# Revit family: NBS_Allermuir_DmstcChrs_Tarry_LoungeChair
name_source: partatom
category: Furniture
revit_build: Autodesk Revit 2017 (Build: 20171027_0315(x64)
units: mm (PartAtom-declared; Revit-internal decimal feet)

## family parameters
Always vertical = Yes
Cut with Voids When Loaded = No
Room Calculation Point = No
Shared = No
Work Plane-Based = No

## types (2) — shared parameters
AssetType = Movable
Category = Pr_40_50_12_22:Dining chairs
CodePerformance = ANSI/BIFMA X5.1: 2017
DurationUnit = year
EnvironmentalProductDeclaration = http://www.thesenatorgroup.com
ExpectedLife = 10
Features = Moulded foam construction with dual density back foam, height adjustable headrest, fully upholstered, solid ash legs with a clear finish, plastic glides,, optional feature: solid ash legs can be stained or colour washed , optional feature: plastic glides with felt, optional feature: two-tone upholstery
FrameColour = Black
FrameFinish = Powder coat
FramesFinish = Clear
FramesMaterial = Solid ash
IfcExportAs = IfcFurnitureType
IfcExportType = CHAIR
IntegralAccessories = Plastic glides
IsBuiltIn = No
ManufacturerName = Allermuir
ManufacturerURL = http://www.allermuir.co.uk
ModelReference = TarryLoungeChair
NBSCertification = www.nationalbimlibrary.com/cert/y25tegts
NBSDescription = Domestic chairs
NBSReference = 45-35-20/365
NominalDepth = 815 mm  [stored 2.67388 ft]
NominalLength = 740 mm  [stored 2.42782 ft]
NominalWidth = 740 mm  [stored 2.42782 ft]
ProductInformation = http://www.allermuir.co.uk
SeatBaseMaterial = NBS_Concept
SeatFrameMaterial = NBS_Concept
SeatingSeatMaterial = NBS_Concept
SeatsAndBacksFinish = Upholstered
SeatsAndBacksMaterial = Upholstered
Status = New
Style = Chair
Uniclass2015Code = Pr_40_50_12_22
Uniclass2015Title = Dining chairs
Uniclass2015Version = Products v1.12
Version = 2
WarrantyDescription = Allermuir warrant that its manufactured products are free from manufacturing defects - in materials or workmanship - for a period of five (5) years. , Allermuir will repair, or replace (at Allermuir's sole discretion) with comparable free of charge materials / components, any product / component which fails under normal use in a single shift environment, as a result of a defect in the materials and/ or workmanship
WarrantyDurationParts = 5
WarrantyDurationUnit = year
Weight = 33 kg
zero-valued in all types: HighestSeatingHeight, LowestSeatingHeight

## per-type parameters (varying)
| type | BIMObjectName | Description | Has4StarSwivelBase | HasWoodLegs | Name | NominalHeight | SeatingHeight | Size |
| TAR405 | NBS_Allermuir_DomesticChairs_TarryLoungeChair_TAR405 | Lounge chair 4-Star Swivel Base | Yes | No | DomesticChairs_TarryLoungeChair_TAR405_Allermuir | 1210 mm  [stored 3.96982 ft] | 410 mm  [stored 1.34514 ft] | 815 x 1260 x 430 x 740 mm |
| TAR403 | NBS_Allermuir_DomesticChairs_TarryLoungeChair_TAR403 | Wing lounge chair with wood legs | No | Yes | DomesticChairs_TarryLoungeChair_TAR403_Allermuir | 1230 mm  [stored 4.03543 ft] | 430 mm | 815 x 1225 x 430 x 740 mm |

note: column(s) folded — value = type name in every type: ModelNumber

note: [stored X ft] marks values corroborated as IEEE doubles in the binary element streams (Revit-internal decimal feet)

## geometry (parser evidence)
native form markers: Sweep x3
no freeform markers — native parametric forms only
